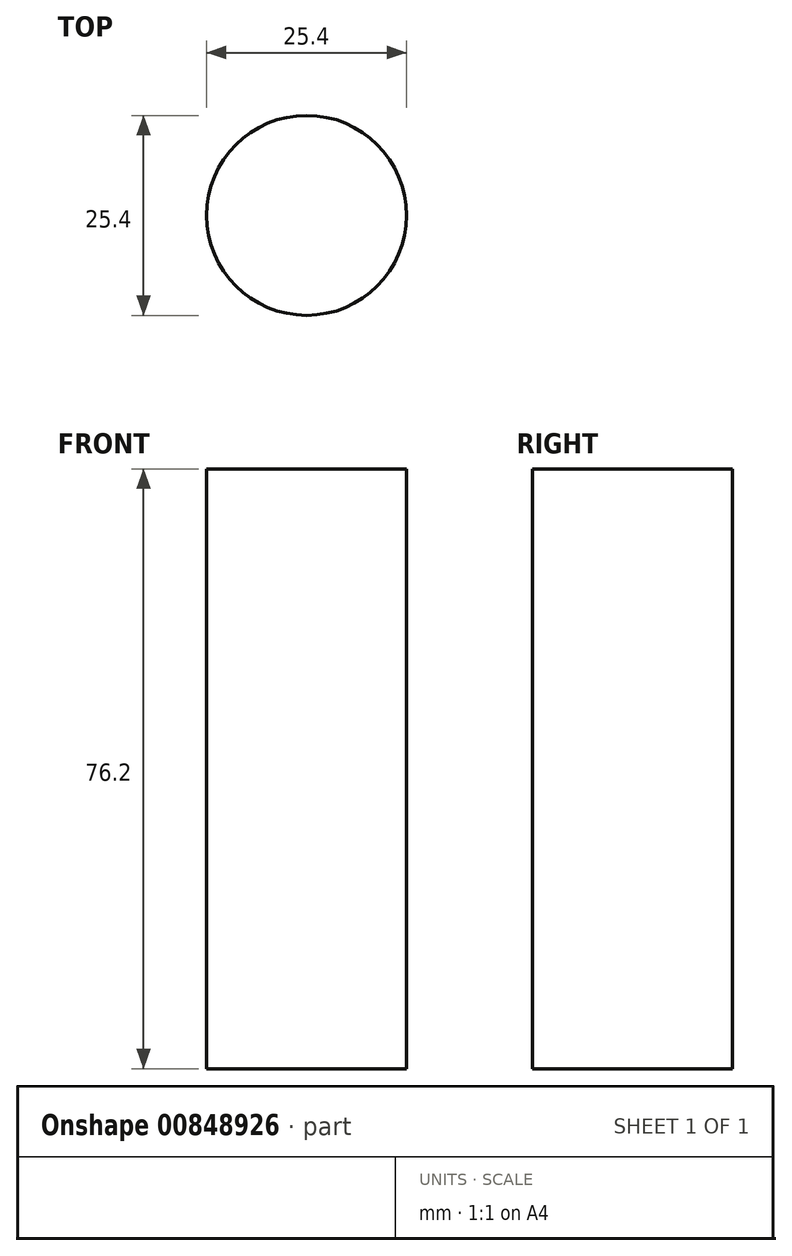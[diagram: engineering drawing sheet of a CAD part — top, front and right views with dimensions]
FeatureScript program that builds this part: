
annotation { "Feature Type Name" : "Feature", "Feature Type Description" : "" }
export const myFeature = defineFeature(function(context is Context, id is Id, definition is map)
    precondition{}
    {
        {
            var Q0;
            Q0=qCreatedBy(makeId("Front.planeOp"),FACE);
            var sketch = newSketch(context, id + "F0", { "sketchPlane" : qUnion([Q0])});
            skLineSegment(sketch, "E0", {"start": v(8.54, -10.71) * mm, "end": v(21.24, -10.71) * mm});
            skLineSegment(sketch, "E1", {"start": v(21.24, -10.71) * mm, "end": v(21.24, 65.49) * mm});
            skLineSegment(sketch, "E2", {"start": v(21.24, 65.49) * mm, "end": v(8.54, 65.49) * mm});
            skLineSegment(sketch, "E3", {"start": v(8.54, 65.49) * mm, "end": v(8.54, -10.71) * mm});
            skSolve(sketch);
        }
        {
            var Q0;
            Q0=makeQuery(id+"F0.imprint","IMPRINT",FACE,{"disambiguationData":[TD([[makeQuery(id+"F0.imprint","IMPRINT",EDGE,{"derivedFrom":sQuery(id+"F0.wireOp",EDGE,"E0")}),1.0]])]});
            var Q1;
            Q1=sQuery(id+"F0.wireOp",EDGE,"E1");
            revolve(context, id + "F1", {"surfaceOperationType" : NewSurfaceOperationType.NEW, "entities" : qUnion([Q0]), "axis" : qUnion([Q1]), "revolveType" : RevolveType.FULL});
        }
    });
